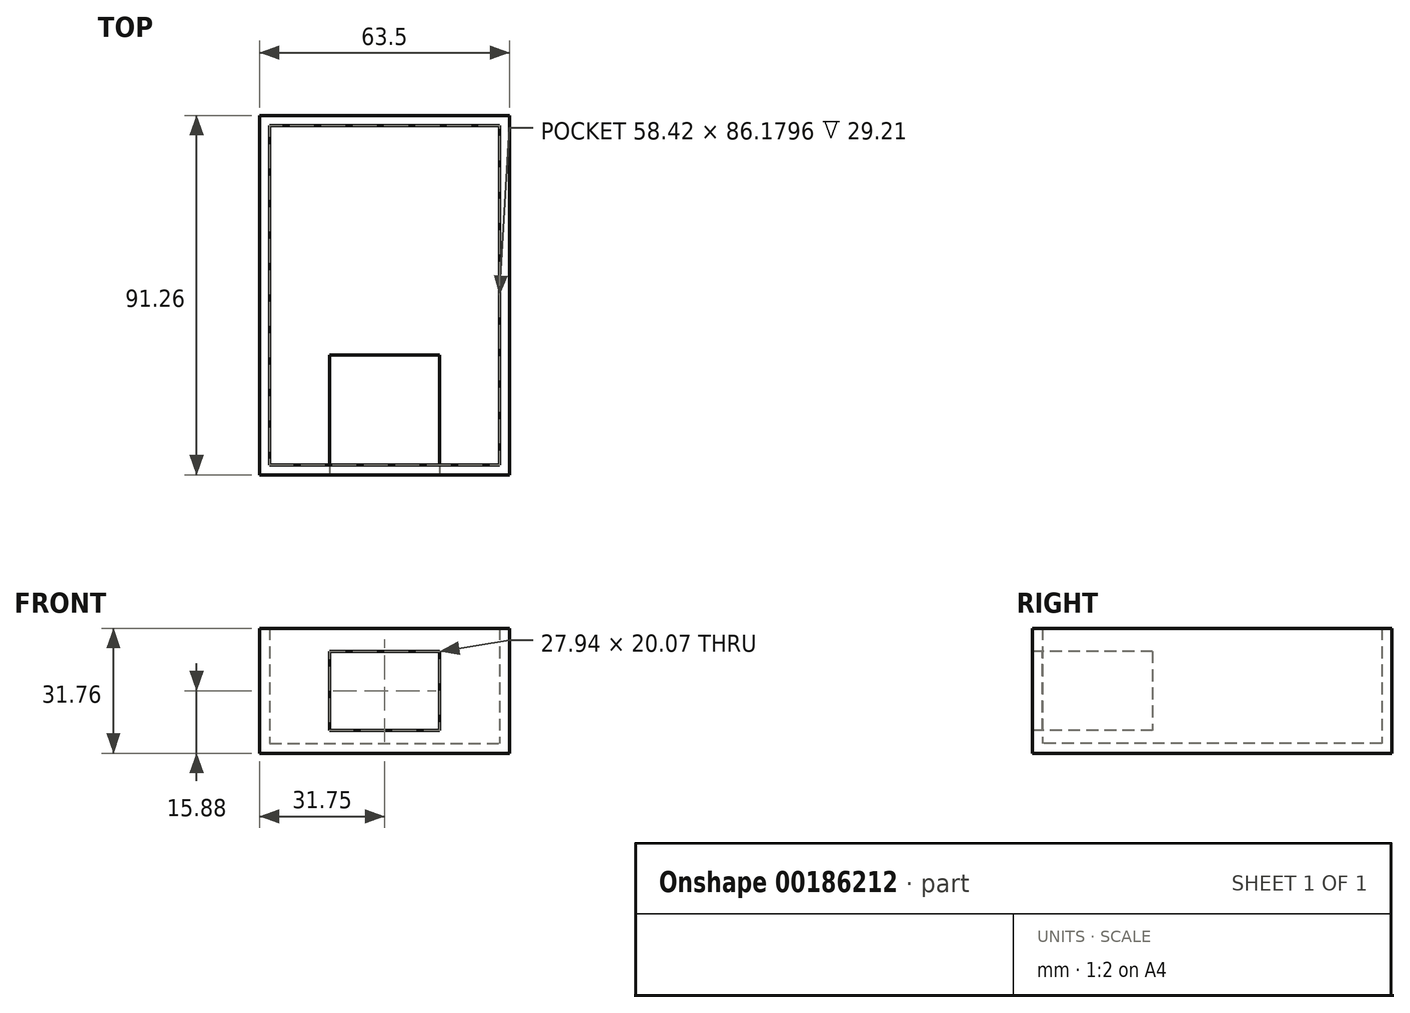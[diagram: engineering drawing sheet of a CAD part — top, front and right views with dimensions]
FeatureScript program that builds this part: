
annotation { "Feature Type Name" : "Feature", "Feature Type Description" : "" }
export const myFeature = defineFeature(function(context is Context, id is Id, definition is map)
    precondition{}
    {
        {
            var Q0;
            Q0=qCreatedBy(makeId("Top.planeOp"),FACE);
            var sketch = newSketch(context, id + "F0", { "sketchPlane" : qUnion([Q0])});
            skLineSegment(sketch, "E0.bottom", {"start": v(-31.75, 45.63) * mm, "end": v(31.75, 45.63) * mm});
            skLineSegment(sketch, "E0.top", {"start": v(-31.75, -45.63) * mm, "end": v(31.75, -45.63) * mm});
            skLineSegment(sketch, "E0.left", {"start": v(-31.75, 45.63) * mm, "end": v(-31.75, -45.63) * mm});
            skLineSegment(sketch, "E0.right", {"start": v(31.75, 45.63) * mm, "end": v(31.75, -45.63) * mm});
            skPoint(sketch, "E0.middle", {"position": v(0, 0) * mm});
            skSolve(sketch);
        }
        {
            var Q0;
            Q0 = qSketchRegion(id + "F0", true);
            extrude(context, id + "F1", {"entities" : qUnion([Q0]), "endBound" : BoundingType.SYMMETRIC, "depth" : 31.75 * mm});
        }
        {
            var Q0;
            Q0=makeQuery(id+"F1.opExtrude","CAP_FACE",FACE,{"disambiguationData":[OSD([sQuery(id+"F0.wireOp",EDGE,"E0.bottom"),sQuery(id+"F0.wireOp",EDGE,"E0.top"),sQuery(id+"F0.wireOp",EDGE,"E0.left"),sQuery(id+"F0.wireOp",EDGE,"E0.right")])],"isStart":false});
            shell(context, id + "F2", {"entities" : qUnion([Q0]), "thickness" : 2.54 * mm});
        }
        {
            var Q0;
            Q0=makeQuery(id+"F1.opExtrude","SWEPT_FACE",FACE,{"disambiguationData":[OSD([sQuery(id+"F0.wireOp",EDGE,"E0.top")])]});
            var sketch = newSketch(context, id + "F3", { "sketchPlane" : qUnion([Q0])});
            skLineSegment(sketch, "E1.bottom", {"start": v(-13.97, 10.03) * mm, "end": v(13.97, 10.03) * mm});
            skLineSegment(sketch, "E1.top", {"start": v(-13.97, -10.03) * mm, "end": v(13.97, -10.03) * mm});
            skLineSegment(sketch, "E1.left", {"start": v(-13.97, 10.03) * mm, "end": v(-13.97, -10.03) * mm});
            skLineSegment(sketch, "E1.right", {"start": v(13.97, 10.03) * mm, "end": v(13.97, -10.03) * mm});
            skPoint(sketch, "E1.middle", {"position": v(0, 0) * mm});
            skSolve(sketch);
        }
        {
            var Q0;
            Q0 = qSketchRegion(id + "F3", true);
            extrude(context, id + "F4", {"entities" : qUnion([Q0]), "operationType" : NewBodyOperationType.REMOVE, "oppositeDirection" : true, "depth" : 6.35 * mm});
        }
        {
            var Q0;
            Q0=makeQuery(id+"F1.opExtrude","SWEPT_FACE",FACE,{"disambiguationData":[OSD([sQuery(id+"F0.wireOp",EDGE,"E0.top")])]});
            var sketch = newSketch(context, id + "F5", { "sketchPlane" : qUnion([Q0])});
            skLineSegment(sketch, "E2.bottom", {"start": v(-13.97, 10.03) * mm, "end": v(13.97, 10.03) * mm});
            skLineSegment(sketch, "E2.top", {"start": v(-13.97, -10.03) * mm, "end": v(13.97, -10.03) * mm});
            skLineSegment(sketch, "E2.left", {"start": v(-13.97, 10.03) * mm, "end": v(-13.97, -10.03) * mm});
            skLineSegment(sketch, "E2.right", {"start": v(13.97, 10.03) * mm, "end": v(13.97, -10.03) * mm});
            skSolve(sketch);
        }
        {
            var Q0;
            Q0 = qSketchRegion(id + "F5", true);
            extrude(context, id + "F6", {"entities" : qUnion([Q0]), "oppositeDirection" : true, "depth" : 30.48 * mm});
        }
    });
